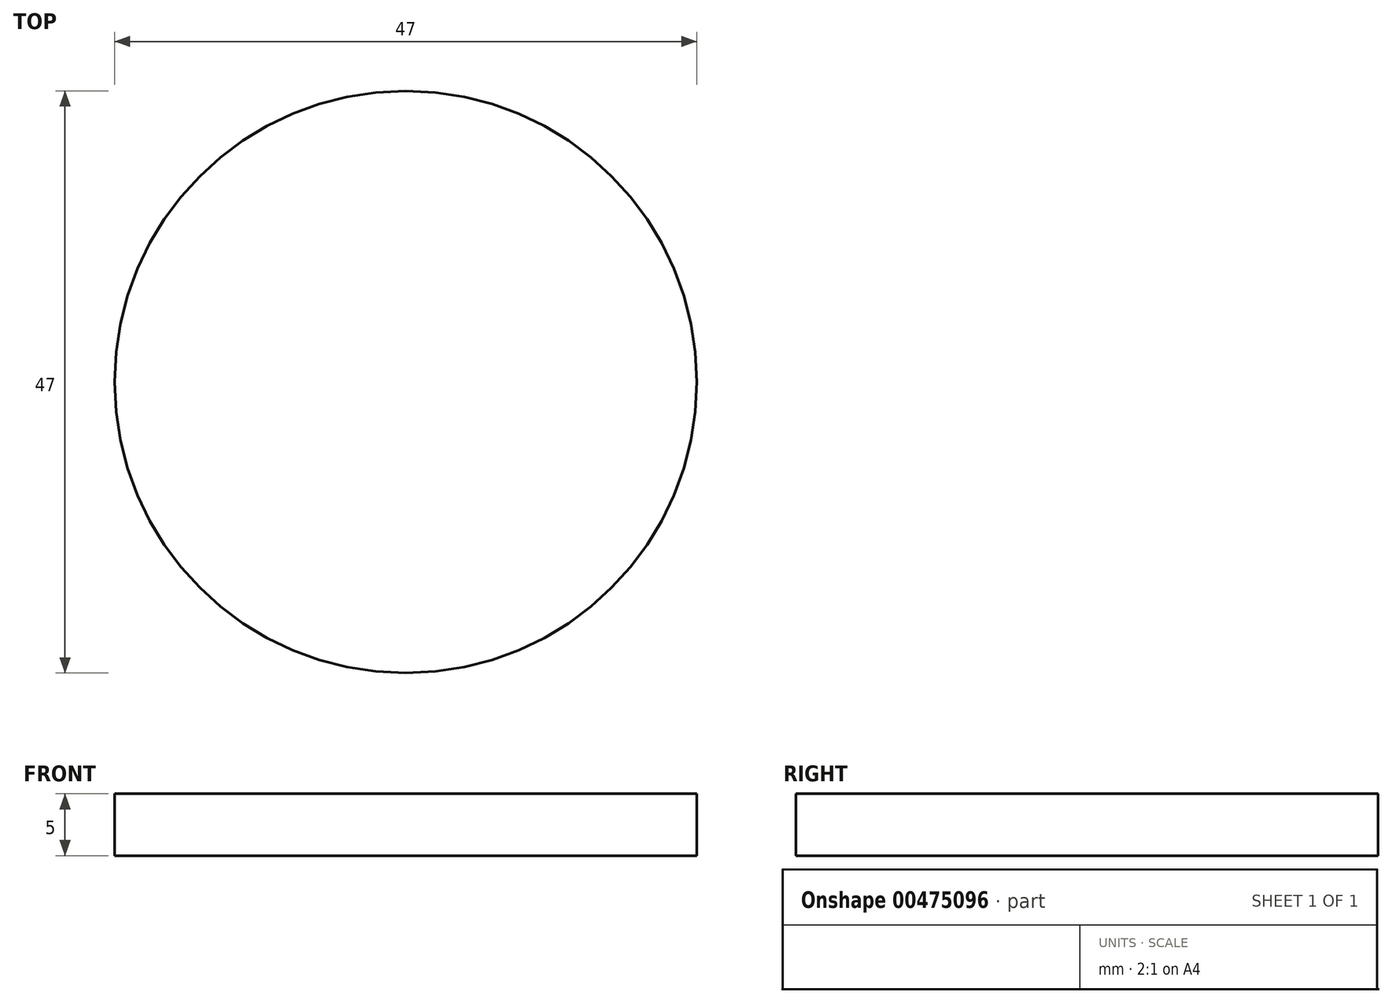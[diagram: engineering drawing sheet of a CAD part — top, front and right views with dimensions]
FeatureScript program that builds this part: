
annotation { "Feature Type Name" : "Feature", "Feature Type Description" : "" }
export const myFeature = defineFeature(function(context is Context, id is Id, definition is map)
    precondition{}
    {
        {
            var Q0;
            Q0=qCreatedBy(makeId("Top.planeOp"),FACE);
            var sketch = newSketch(context, id + "F0", { "sketchPlane" : qUnion([Q0])});
            skCircle(sketch, "E0", {"center": v(0, 0) * mm, "radius": 23.5 * mm});
            skSolve(sketch);
        }
        {
            var Q0;
            Q0 = qSketchRegion(id + "F0", true);
            extrude(context, id + "F1", {"entities" : qUnion([Q0]), "depth" : 5 * mm});
        }
    });
